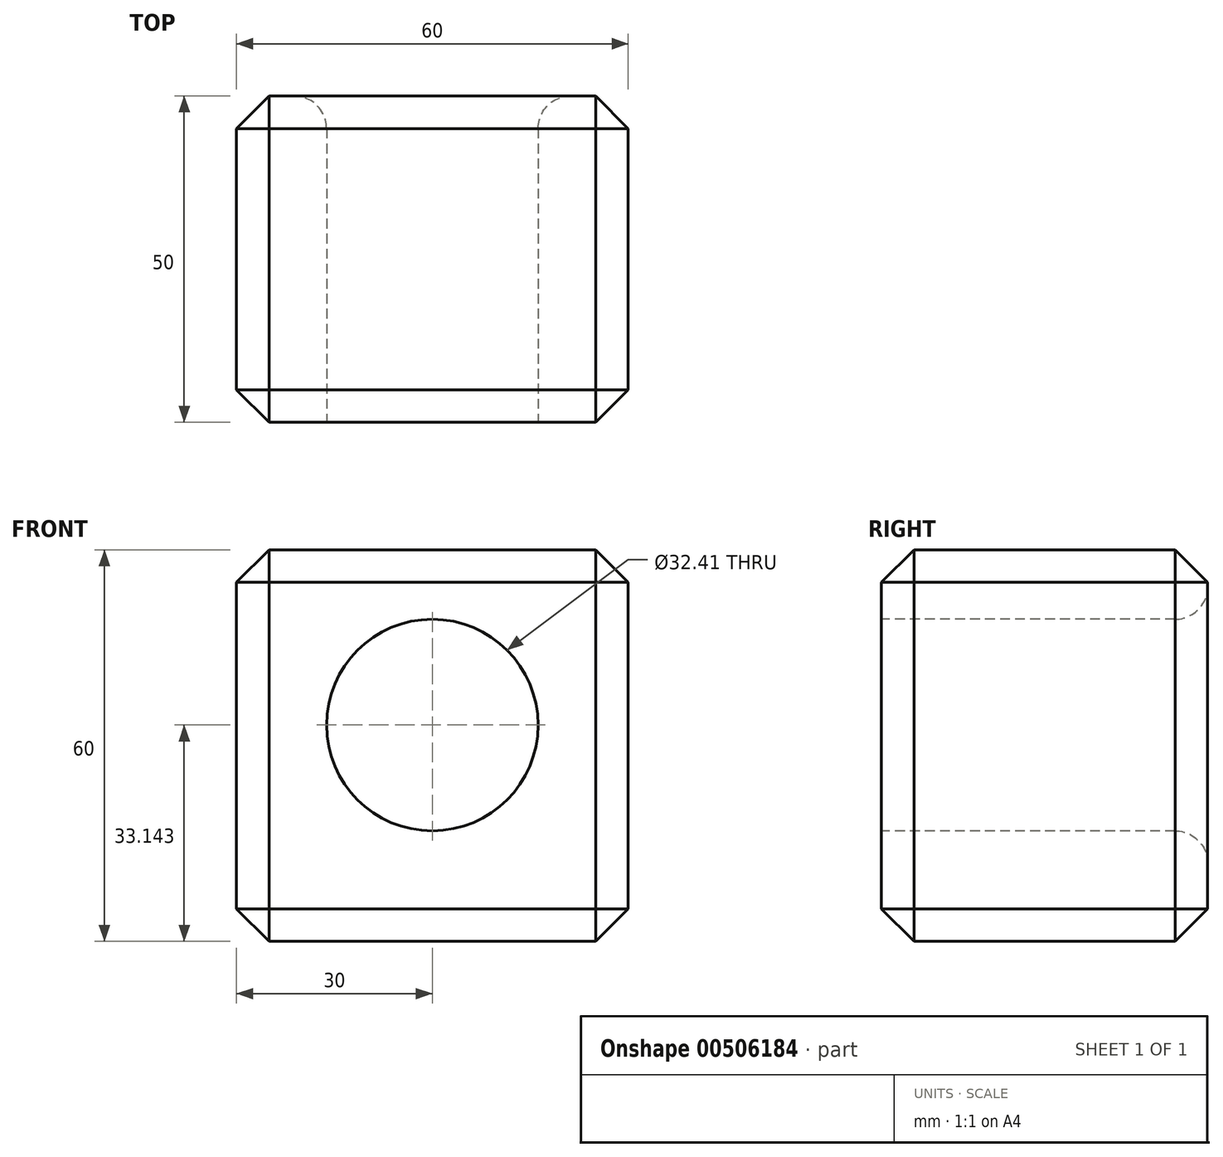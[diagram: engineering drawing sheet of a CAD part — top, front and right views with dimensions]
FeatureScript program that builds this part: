
annotation { "Feature Type Name" : "Feature", "Feature Type Description" : "" }
export const myFeature = defineFeature(function(context is Context, id is Id, definition is map)
    precondition{}
    {
        {
            var Q0;
            Q0=qCreatedBy(makeId("Top.planeOp"),FACE);
            var sketch = newSketch(context, id + "F0", { "sketchPlane" : qUnion([Q0])});
            skLineSegment(sketch, "E0.bottom", {"start": v(30, 25) * mm, "end": v(-30, 25) * mm});
            skLineSegment(sketch, "E0.top", {"start": v(30, -25) * mm, "end": v(-30, -25) * mm});
            skLineSegment(sketch, "E0.left", {"start": v(30, 25) * mm, "end": v(30, -25) * mm});
            skLineSegment(sketch, "E0.right", {"start": v(-30, 25) * mm, "end": v(-30, -25) * mm});
            skPoint(sketch, "E0.middle", {"position": v(0, 0) * mm});
            skSolve(sketch);
        }
        {
            var Q0;
            Q0=makeQuery(id+"F0.imprint","IMPRINT",FACE,{"disambiguationData":[TD([[makeQuery(id+"F0.imprint","IMPRINT",EDGE,{"derivedFrom":sQuery(id+"F0.wireOp",EDGE,"E0.bottom")}),1.0]])]});
            extrude(context, id + "F1", {"entities" : qUnion([Q0]), "depth" : 60 * mm});
        }
        {
            var Q0;
            Q0=makeQuery(id+"F1.opExtrude","SWEPT_FACE",FACE,{"disambiguationData":[OSD([sQuery(id+"F0.wireOp",EDGE,"E0.top")])]});
            var sketch = newSketch(context, id + "F2", { "sketchPlane" : qUnion([Q0])});
            skCircle(sketch, "E1", {"center": v(0, 33.14) * mm, "radius": 16.2 * mm});
            skSolve(sketch);
        }
        {
            var Q0;
            Q0 = qSketchRegion(id + "F2", true);
            extrude(context, id + "F3", {"entities" : qUnion([Q0]), "operationType" : NewBodyOperationType.REMOVE, "endBound" : BoundingType.THROUGH_ALL, "oppositeDirection" : true, "depth" : 25 * mm});
        }
        {
            var Q0;
            Q0=makeQuery(id+"F3.boolean.opBoolean","COPY",EDGE,{"derivedFrom":makeQuery(id+"F3.opExtrude","CAP_EDGE",EDGE,{"disambiguationData":[OSD([sQuery(id+"F2.wireOp",EDGE,"E1")])],"isStart":true})});
            var Q1;
            Q1=makeQuery(id+"F3.boolean.opBoolean","INTERSECT",EDGE,{"derivedFrom":[makeQuery(id+"F1.opExtrude","SWEPT_FACE",FACE,{"disambiguationData":[OSD([sQuery(id+"F0.wireOp",EDGE,"E0.bottom")])]}),makeQuery(id+"F3.opExtrude","SWEPT_FACE",FACE,{"disambiguationData":[OSD([sQuery(id+"F2.wireOp",EDGE,"E1")])]})]});
            fillet(context, id + "F4", {"entities" : qUnion([Q0, Q1]), "radius" : 5 * mm, "tangentPropagation" : true, "allowEdgeOverflow" : false});
        }
        {
            var Q0;
            Q0=makeQuery(id+"F1.opExtrude","SWEPT_EDGE",EDGE,{"disambiguationData":[OSD([sQuery(id+"F0.wireOp",EDGE,"E0.bottom"),sQuery(id+"F0.wireOp",EDGE,"E0.right")])]});
            var Q1;
            Q1=makeQuery(id+"F1.opExtrude","SWEPT_EDGE",EDGE,{"disambiguationData":[OSD([sQuery(id+"F0.wireOp",EDGE,"E0.top"),sQuery(id+"F0.wireOp",EDGE,"E0.right")])]});
            var Q2;
            Q2=makeQuery(id+"F1.opExtrude","CAP_EDGE",EDGE,{"disambiguationData":[OSD([sQuery(id+"F0.wireOp",EDGE,"E0.right")])],"isStart":false});
            var Q3;
            Q3=makeQuery(id+"F1.opExtrude","CAP_EDGE",EDGE,{"disambiguationData":[OSD([sQuery(id+"F0.wireOp",EDGE,"E0.bottom")])],"isStart":false});
            var Q4;
            Q4=makeQuery(id+"F1.opExtrude","CAP_EDGE",EDGE,{"disambiguationData":[OSD([sQuery(id+"F0.wireOp",EDGE,"E0.top")])],"isStart":false});
            var Q5;
            Q5=makeQuery(id+"F1.opExtrude","CAP_EDGE",EDGE,{"disambiguationData":[OSD([sQuery(id+"F0.wireOp",EDGE,"E0.top")])],"isStart":true});
            var Q6;
            Q6=makeQuery(id+"F1.opExtrude","CAP_EDGE",EDGE,{"disambiguationData":[OSD([sQuery(id+"F0.wireOp",EDGE,"E0.right")])],"isStart":true});
            var Q7;
            Q7=makeQuery(id+"F1.opExtrude","SWEPT_EDGE",EDGE,{"disambiguationData":[OSD([sQuery(id+"F0.wireOp",EDGE,"E0.top"),sQuery(id+"F0.wireOp",EDGE,"E0.left")])]});
            var Q8;
            Q8=makeQuery(id+"F1.opExtrude","CAP_EDGE",EDGE,{"disambiguationData":[OSD([sQuery(id+"F0.wireOp",EDGE,"E0.left")])],"isStart":false});
            var Q9;
            Q9=makeQuery(id+"F1.opExtrude","SWEPT_EDGE",EDGE,{"disambiguationData":[OSD([sQuery(id+"F0.wireOp",EDGE,"E0.bottom"),sQuery(id+"F0.wireOp",EDGE,"E0.left")])]});
            var Q10;
            Q10=makeQuery(id+"F1.opExtrude","CAP_EDGE",EDGE,{"disambiguationData":[OSD([sQuery(id+"F0.wireOp",EDGE,"E0.left")])],"isStart":true});
            var Q11;
            Q11=makeQuery(id+"F1.opExtrude","CAP_EDGE",EDGE,{"disambiguationData":[OSD([sQuery(id+"F0.wireOp",EDGE,"E0.bottom")])],"isStart":true});
            chamfer(context, id + "F5", {"entities" : qUnion([Q0, Q1, Q2, Q3, Q4, Q5, Q6, Q7, Q8, Q9, Q10, Q11]), "width" : 5 * mm, "tangentPropagation" : true});
        }
    });
